# Revit family: STERN FAUCETS_Quadrat DM SD
name_source: partatom
category: Generic Models
units: mm (PartAtom-declared; Revit-internal decimal feet)

## family parameters
Can host rebar = No
Cut with Voids When Loaded = No
Host = Face
Part Type = Normal
Room Calculation Point = Yes
Round Connector Dimension = Use Diameter
Shared = No

## types (2) — shared parameters
BADGE = https://bim.archiproducts.com
DEPTH = 120 mm
Default Elevation = 1219 mm
Description = Quadrat DM SD - Touch-free electronic soap dispenser for deckmounted
installations. Activated by infrared sensor.
For use with any non-proprietary soap. Chrome
plated body, other finishes available. Includes
a 1 liter soap bottle and bottle support.
FINISHING MATERIAL = Chrome - Stern
HEIGHT = 100 mm  [stored 0.328084 ft]
INSTALLATION = Deck mounted
MATERIAL DESCRIPTION = Finish: Chrome (other finishes avaiable)
MOUNTING OFFSET = 14 mm  [stored 0.0459318 ft]
Manufacturer = Stern Engineering
Model = Quadrat DM SD
OPTIONS = Remote control (code 07100008), Matching battery-powered faucet (Upon request), Matching transformer-powered faucet (code 351010), 6-pack: 6 soap dispensers and a remote control (Upon request), Multifeed system (Upon request)
PRODUCT SHEET = https://www.archiproducts.com
REFILL = Soap priming operated by remote control or by easy-to-use manual refill button
SOAP = 1 Liter soap bottle.
Peristaltic pump enables the use of any kind of liquid soap, detergent or antibacterial gel
SOAP DOSE = Default setting: 1.2-1.6 cc
Adjustable by remote control in accordance to the selected soap.
Adjustable by remote control in accordance to the selected soap
Adjustable by remote control in accordance to the selected soap
TECHNICAL SHEET = https://www.sternfaucets.com
URL = http://www.sternfaucets.com
VOLTAGE = 12 V
WIDTH = 25 mm  [stored 0.082021 ft]

## per-type parameters (varying)
| type | POWER SUPPLY | PRODUCT CODE |
| QUADRAT DM SD - 12V TRANSFORMER | 12V transformer | 351952 (E) |
| QUADRAT DM SD - 12V BATTERY | 12V battery | 351950 (B) |

note: [stored X ft] marks values corroborated as IEEE doubles in the binary element streams (Revit-internal decimal feet)

## geometry (parser evidence)
native form markers: Blend x4, Sweep x2
no freeform markers — native parametric forms only
